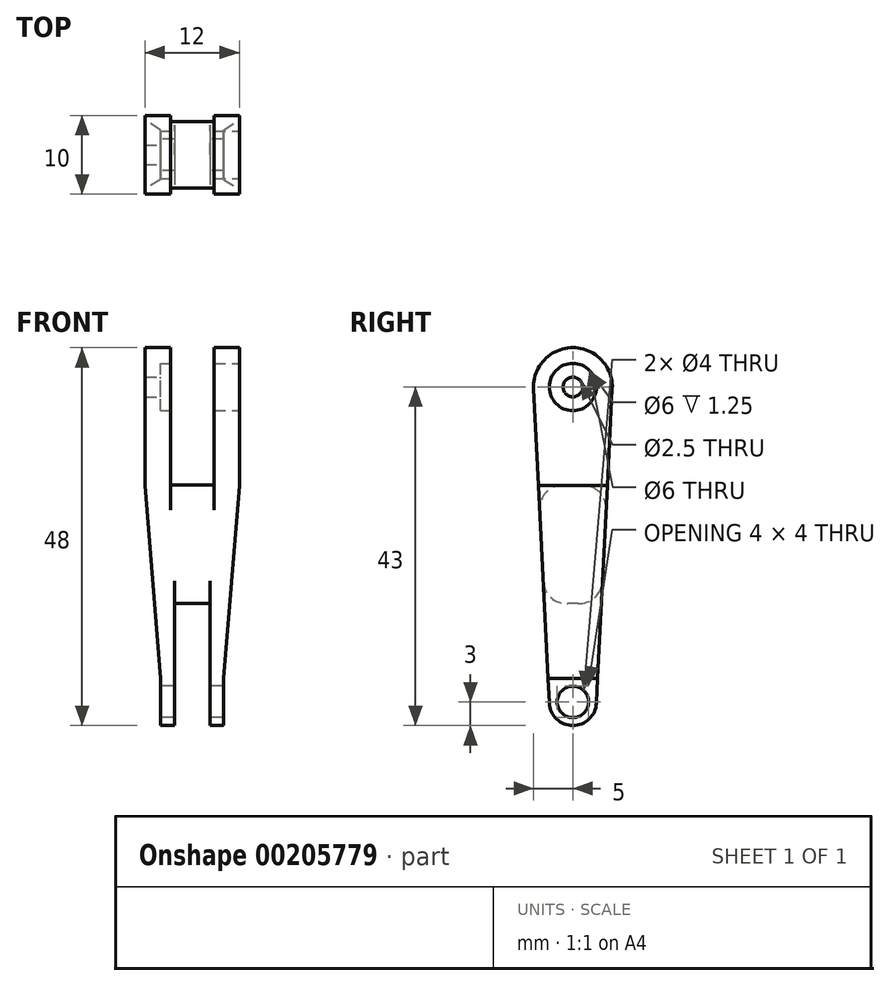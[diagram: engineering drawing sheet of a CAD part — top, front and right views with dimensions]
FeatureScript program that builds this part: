
annotation { "Feature Type Name" : "Feature", "Feature Type Description" : "" }
export const myFeature = defineFeature(function(context is Context, id is Id, definition is map)
    precondition{}
    {
        {
            var Q0;
            Q0=qCreatedBy(makeId("Right.planeOp"),FACE);
            var sketch = newSketch(context, id + "F0", { "sketchPlane" : qUnion([Q0])});
            skCircle(sketch, "E0", {"center": v(0, 0) * mm, "radius": 1 * mm});
            skCircle(sketch, "E1", {"center": v(0, -40) * mm, "radius": 2 * mm});
            skArc(sketch, "E2", {"start": v(5, -0.25) * mm, "mid": v(0, 5) * mm, "end": v(-5, -0.25) * mm});
            skArc(sketch, "E3", {"start": v(-3, -40.15) * mm, "mid": v(0, -43) * mm, "end": v(3, -40.15) * mm});
            skLineSegment(sketch, "E4", {"start": v(-5, -0.25) * mm, "end": v(-3, -40.15) * mm});
            skLineSegment(sketch, "E5", {"start": v(0, 0) * mm, "end": v(0, -40) * mm, "construction": true});
            skLineSegment(sketch, "E6.MirrorCS", {"start": v(5, -0.25) * mm, "end": v(3, -40.15) * mm});
            skSolve(sketch);
        }
        {
            var Q0;
            Q0 = qSketchRegion(id + "F0", true);
            extrude(context, id + "F1", {"entities" : qUnion([Q0]), "depth" : 12 * mm, "symmetric" : true});
        }
        {
            var Q0;
            Q0=qCreatedBy(makeId("Front.planeOp"),FACE);
            var sketch = newSketch(context, id + "F2", { "sketchPlane" : qUnion([Q0])});
            skLineSegment(sketch, "E7", {"start": v(-2.75, 12.5) * mm, "end": v(-2.75, 3) * mm});
            skLineSegment(sketch, "E8", {"start": v(-2.75, 3) * mm, "end": v(-4, 3) * mm});
            skLineSegment(sketch, "E9", {"start": v(-6, 0) * mm, "end": v(6, 0) * mm, "construction": true});
            skLineSegment(sketch, "E10", {"start": v(-4, 3) * mm, "end": v(-4, 1.25) * mm});
            skLineSegment(sketch, "E11", {"start": v(-4, 1.25) * mm, "end": v(-6, 1.25) * mm});
            skLineSegment(sketch, "E12", {"start": v(-2.75, 12.5) * mm, "end": v(2.75, 12.5) * mm});
            skLineSegment(sketch, "E13", {"start": v(0, 0) * mm, "end": v(0, 12.5) * mm, "construction": true});
            skPoint(sketch, "E13.endSnap0", {"position": v(0, 12.5) * mm});
            skLineSegment(sketch, "E14", {"start": v(2.75, 12.5) * mm, "end": v(2.75, 3) * mm});
            skLineSegment(sketch, "E15", {"start": v(2.75, 3) * mm, "end": v(6, 3) * mm});
            skLineSegment(sketch, "E16", {"start": v(6, 3) * mm, "end": v(6, 0) * mm});
            skLineSegment(sketch, "E17", {"start": v(-6, 1.25) * mm, "end": v(-6, 0) * mm});
            skLineSegment(sketch, "E18", {"start": v(-2.75, 3) * mm, "end": v(2.75, 3) * mm, "construction": true});
            skLineSegment(sketch, "E19", {"start": v(-6, 0) * mm, "end": v(6, 0) * mm});
            skSolve(sketch);
        }
        {
            var Q0;
            Q0 = qSketchRegion(id + "F2", true);
            var Q1;
            Q1=sQuery(id+"F2.wireOp",EDGE,"E19");
            revolve(context, id + "F3", {"operationType" : NewBodyOperationType.REMOVE, "entities" : qUnion([Q0]), "axis" : qUnion([Q1]), "revolveType" : RevolveType.FULL, "oppositeDirection" : true});
        }
        {
            var Q0;
            Q0=qCreatedBy(makeId("Front.planeOp"),FACE);
            var sketch = newSketch(context, id + "F4", { "sketchPlane" : qUnion([Q0])});
            skLineSegment(sketch, "E20", {"start": v(0, -40) * mm, "end": v(-6, -40) * mm, "construction": true});
            skLineSegment(sketch, "E21", {"start": v(0, 0) * mm, "end": v(0, -40) * mm, "construction": true});
            skLineSegment(sketch, "E22", {"start": v(0, -52.5) * mm, "end": v(-2.25, -52.5) * mm});
            skLineSegment(sketch, "E23", {"start": v(-2.25, -52.5) * mm, "end": v(-2.25, -42) * mm});
            skLineSegment(sketch, "E24", {"start": v(-2.25, -42) * mm, "end": v(-6, -42) * mm});
            skLineSegment(sketch, "E25", {"start": v(-6, -42) * mm, "end": v(-6, -40) * mm});
            skLineSegment(sketch, "E26.MirrorCS", {"start": v(-2.25, -147.5) * mm, "end": v(-2.25, -158) * mm});
            skLineSegment(sketch, "E27.MirrorCS", {"start": v(-2.25, -158) * mm, "end": v(-6, -158) * mm});
            skLineSegment(sketch, "E28.MirrorCS", {"start": v(-6, -158) * mm, "end": v(-6, -160) * mm});
            skLineSegment(sketch, "E29.MirrorCS", {"start": v(0, -147.5) * mm, "end": v(-2.25, -147.5) * mm});
            skLineSegment(sketch, "E30.MirrorCS", {"start": v(0, -200) * mm, "end": v(0, -160) * mm, "construction": true});
            skLineSegment(sketch, "E31.MirrorCS", {"start": v(6, -42) * mm, "end": v(6, -40) * mm});
            skLineSegment(sketch, "E32.MirrorCS", {"start": v(2.25, -42) * mm, "end": v(6, -42) * mm});
            skLineSegment(sketch, "E33.MirrorCS", {"start": v(2.25, -52.5) * mm, "end": v(2.25, -42) * mm});
            skLineSegment(sketch, "E34.MirrorCS", {"start": v(0, -52.5) * mm, "end": v(2.25, -52.5) * mm});
            skLineSegment(sketch, "E35.MirrorCS", {"start": v(0, -40) * mm, "end": v(6, -40) * mm, "construction": true});
            skLineSegment(sketch, "E36", {"start": v(-2.25, -42) * mm, "end": v(2.25, -42) * mm, "construction": true});
            skLineSegment(sketch, "E37", {"start": v(-6, -40) * mm, "end": v(6, -40) * mm});
            skSolve(sketch);
        }
        {
            var Q0;
            Q0=makeQuery(id+"F4.imprint","IMPRINT",FACE,{"disambiguationData":[TD([[makeQuery(id+"F4.imprint","IMPRINT",EDGE,{"derivedFrom":sQuery(id+"F4.wireOp",EDGE,"E22")}),-1.0]])]});
            var Q1;
            Q1=sQuery(id+"F4.wireOp",EDGE,"E37");
            revolve(context, id + "F5", {"operationType" : NewBodyOperationType.REMOVE, "entities" : qUnion([Q0]), "axis" : qUnion([Q1]), "revolveType" : RevolveType.FULL, "oppositeDirection" : true});
        }
        {
            var Q0;
            Q0=qCreatedBy(makeId("Front.planeOp"),FACE);
            var sketch = newSketch(context, id + "F6", { "sketchPlane" : qUnion([Q0])});
            skLineSegment(sketch, "E38", {"start": v(0, -43) * mm, "end": v(-4, -43) * mm});
            skLineSegment(sketch, "E39", {"start": v(-4, -43) * mm, "end": v(-4, -37) * mm});
            skLineSegment(sketch, "E40", {"start": v(-4, -37) * mm, "end": v(-6, -12.5) * mm});
            skLineSegment(sketch, "E41", {"start": v(-6, -12.5) * mm, "end": v(-6, 5) * mm});
            skLineSegment(sketch, "E42", {"start": v(-6, 5) * mm, "end": v(0, 5) * mm});
            skLineSegment(sketch, "E43", {"start": v(0, 5) * mm, "end": v(0, -43) * mm, "construction": true});
            skLineSegment(sketch, "E44.MirrorCS", {"start": v(0, -43) * mm, "end": v(4, -43) * mm});
            skLineSegment(sketch, "E45.MirrorCS", {"start": v(4, -43) * mm, "end": v(4, -37) * mm});
            skLineSegment(sketch, "E46.MirrorCS", {"start": v(4, -37) * mm, "end": v(6, -12.5) * mm});
            skLineSegment(sketch, "E47.MirrorCS", {"start": v(6, -12.5) * mm, "end": v(6, 5) * mm});
            skLineSegment(sketch, "E48.MirrorCS", {"start": v(6, 5) * mm, "end": v(0, 5) * mm});
            skSolve(sketch);
        }
        {
            var Q0;
            Q0 = qSketchRegion(id + "F6", true);
            extrude(context, id + "F7", {"entities" : qUnion([Q0]), "operationType" : NewBodyOperationType.INTERSECT, "endBound" : BoundingType.THROUGH_ALL, "depth" : 25 * mm, "hasSecondDirection" : true, "secondDirectionBound" : BoundingType.THROUGH_ALL, "secondDirectionOppositeDirection" : true, "secondDirectionDepth" : 25 * mm});
        }
        {
            var Q0;
            Q0=makeQuery(id+"F3.boolean.opBoolean","INTERSECT",EDGE,{"derivedFrom":[makeQuery(id+"F1.opExtrude","SWEPT_FACE",FACE,{"disambiguationData":[OSD([sQuery(id+"F0.wireOp",EDGE,"E4")])]}),makeQuery(id+"F3.opRevolve","SWEPT_FACE",FACE,{"disambiguationData":[OSD([sQuery(id+"F2.wireOp",EDGE,"E12")])]})]});
            var Q1;
            Q1=makeQuery(id+"F3.boolean.opBoolean","INTERSECT",EDGE,{"derivedFrom":[makeQuery(id+"F1.opExtrude","SWEPT_FACE",FACE,{"disambiguationData":[OSD([sQuery(id+"F0.wireOp",EDGE,"E6.MirrorCS")])]}),makeQuery(id+"F3.opRevolve","SWEPT_FACE",FACE,{"disambiguationData":[OSD([sQuery(id+"F2.wireOp",EDGE,"E12")])]})]});
            var Q2;
            Q2=makeQuery(id+"F5.boolean.opBoolean","INTERSECT",EDGE,{"derivedFrom":[makeQuery(id+"F1.opExtrude","SWEPT_FACE",FACE,{"disambiguationData":[OSD([sQuery(id+"F0.wireOp",EDGE,"E6.MirrorCS")])]}),makeQuery(id+"F5.opRevolve","SWEPT_FACE",FACE,{"disambiguationData":[OSD([sQuery(id+"F4.wireOp",EDGE,"E22"),sQuery(id+"F4.wireOp",EDGE,"E34.MirrorCS")])]})]});
            var Q3;
            Q3=makeQuery(id+"F5.boolean.opBoolean","INTERSECT",EDGE,{"derivedFrom":[makeQuery(id+"F1.opExtrude","SWEPT_FACE",FACE,{"disambiguationData":[OSD([sQuery(id+"F0.wireOp",EDGE,"E4")])]}),makeQuery(id+"F5.opRevolve","SWEPT_FACE",FACE,{"disambiguationData":[OSD([sQuery(id+"F4.wireOp",EDGE,"E22"),sQuery(id+"F4.wireOp",EDGE,"E34.MirrorCS")])]})]});
            fillet(context, id + "F8", {"entities" : qUnion([Q0, Q1, Q2, Q3]), "radius" : 3 * mm, "tangentPropagation" : true, "allowEdgeOverflow" : false});
        }
    });
